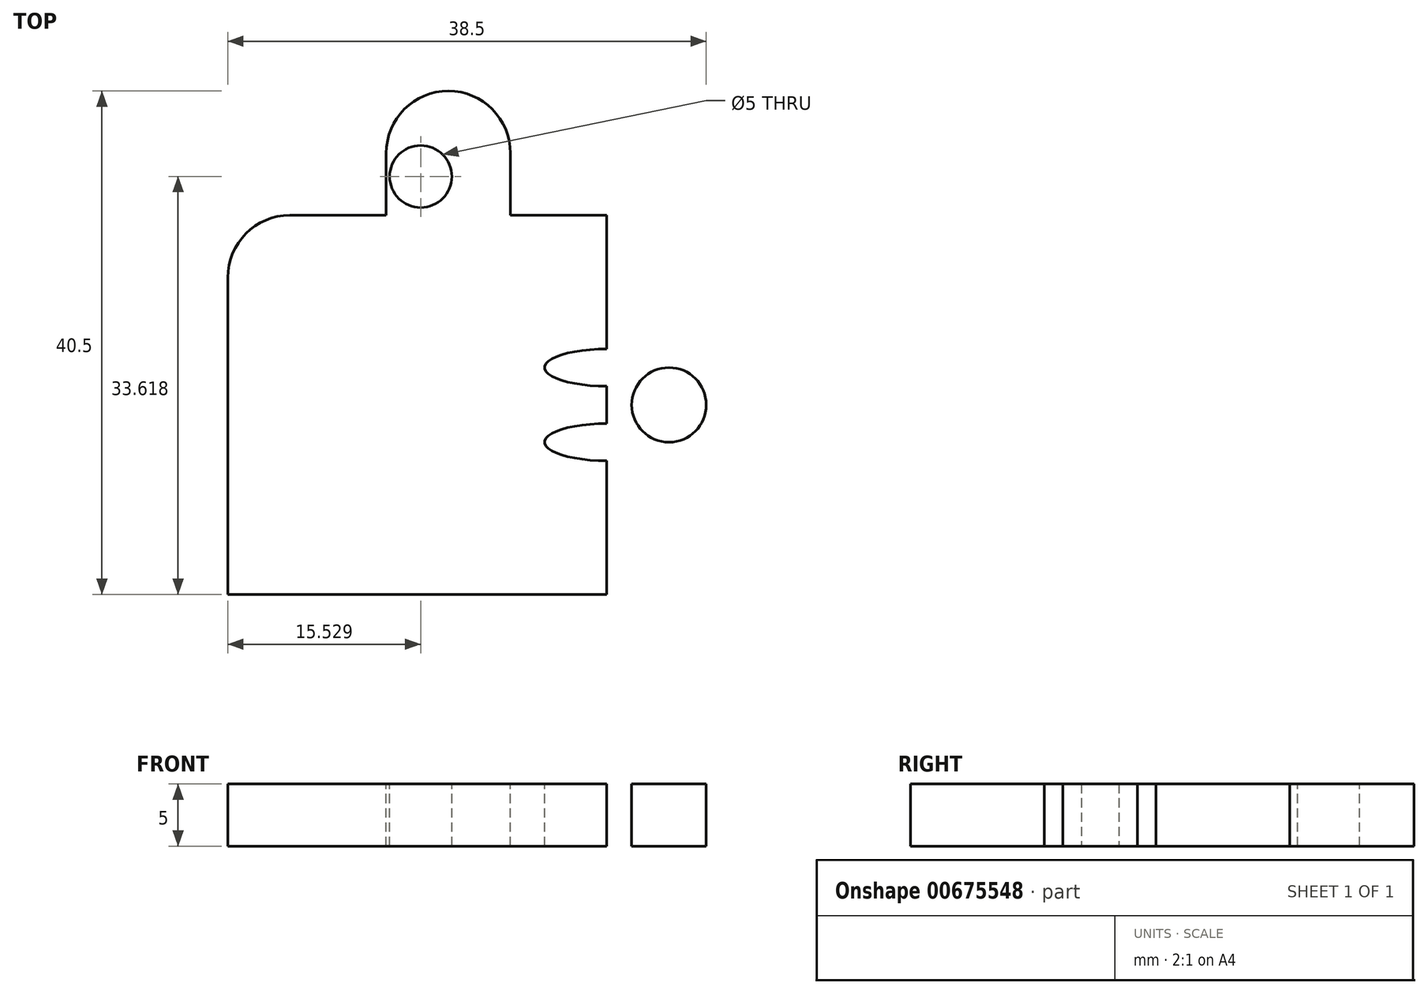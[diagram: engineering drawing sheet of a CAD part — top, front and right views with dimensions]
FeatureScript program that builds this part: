
annotation { "Feature Type Name" : "Feature", "Feature Type Description" : "" }
export const myFeature = defineFeature(function(context is Context, id is Id, definition is map)
    precondition{}
    {
        {
            var Q0;
            Q0=qCreatedBy(makeId("Top.planeOp"),FACE);
            var sketch = newSketch(context, id + "F0", { "sketchPlane" : qUnion([Q0])});
            skLineSegment(sketch, "E0.top", {"start": v(-30.3, -3.55) * mm, "end": v(6.31, -3.55) * mm});
            skPoint(sketch, "E1", {"position": v(2.22, 15.69) * mm});
            skPoint(sketch, "E1.positionSnap0", {"position": v(-28.28, 15.69) * mm});
            skPoint(sketch, "E1.positionSnap1", {"position": v(2.22, 46.19) * mm});
            skLineSegment(sketch, "E2", {"start": v(2.22, 46.19) * mm, "end": v(2.22, 15.69) * mm});
            skLineSegment(sketch, "E3", {"start": v(-28.28, 15.69) * mm, "end": v(2.22, 15.69) * mm});
            skLineSegment(sketch, "E4", {"start": v(-28.28, 15.69) * mm, "end": v(-28.28, 46.19) * mm});
            skLineSegment(sketch, "E5", {"start": v(-28.28, 46.19) * mm, "end": v(2.22, 46.19) * mm});
            skLineSegment(sketch, "E6", {"start": v(2.22, 30.94) * mm, "end": v(2.22, 33.94) * mm});
            skLineSegment(sketch, "E7", {"start": v(2.22, 33.94) * mm, "end": v(2.22, 30.94) * mm});
            skLineSegment(sketch, "E8", {"start": v(2.22, 30.94) * mm, "end": v(2.22, 27.94) * mm});
            skLineSegment(sketch, "E9", {"start": v(2.22, 30.94) * mm, "end": v(2.22, 32.44) * mm});
            skLineSegment(sketch, "E10", {"start": v(2.22, 32.44) * mm, "end": v(2.22, 30.94) * mm});
            skLineSegment(sketch, "E11", {"start": v(2.22, 27.94) * mm, "end": v(2.22, 29.44) * mm});
            skEllipse(sketch, "E12", {"center": v(2.22, 27.94) * mm, "majorRadius": 1.5 * mm, "minorRadius": 5 * mm, "majorAxis": v(0, 1)});
            skEllipse(sketch, "E13", {"center": v(2.22, 33.94) * mm, "majorRadius": 1.5 * mm, "minorRadius": 5 * mm, "majorAxis": v(0, -1)});
            skLineSegment(sketch, "E14", {"start": v(2.22, 30.94) * mm, "end": v(9.22, 30.94) * mm});
            skLineSegment(sketch, "E15", {"start": v(7.22, 27.94) * mm, "end": v(7.22, 33.94) * mm});
            skEllipse(sketch, "E16", {"center": v(7.22, 30.94) * mm, "majorRadius": 3 * mm, "minorRadius": 3 * mm, "majorAxis": v(0, 1)});
            skSolve(sketch);
        }
        {
            var Q0;
            {var subQ0=sQuery(id+"F0.wireOp",EDGE,"E3");Q0=makeQuery(id+"F0.imprint","IMPRINT",FACE,{"disambiguationData":[TD([[makeQuery(id+"F0.imprint","IMPRINT",EDGE,{"derivedFrom":subQ0}),1.0]])]});}
            var Q1;
            {var subQ0=sQuery(id+"F0.wireOp",EDGE,"E7");Q1=makeQuery(id+"F0.imprint","IMPRINT",FACE,{"disambiguationData":[TD([[makeQuery(id+"F0.imprint","IMPRINT",EDGE,{"derivedFrom":subQ0}),-1.0]])]});}
            var Q2;
            {var subQ0=sQuery(id+"F0.wireOp",EDGE,"E11");Q2=makeQuery(id+"F0.imprint","IMPRINT",FACE,{"disambiguationData":[TD([[makeQuery(id+"F0.imprint","IMPRINT",EDGE,{"derivedFrom":subQ0}),1.0]])]});}
            var Q3;
            {var subQ0=sQuery(id+"F0.wireOp",EDGE,"E8");Q3=makeQuery(id+"F0.imprint","IMPRINT",FACE,{"disambiguationData":[TD([[makeQuery(id+"F0.imprint","IMPRINT",EDGE,{"derivedFrom":subQ0}),1.0]])]});}
            var Q4;
            {var subQ0=sQuery(id+"F0.wireOp",EDGE,"E10");Q4=makeQuery(id+"F0.imprint","IMPRINT",FACE,{"disambiguationData":[TD([[makeQuery(id+"F0.imprint","IMPRINT",EDGE,{"derivedFrom":subQ0}),1.0]])]});}
            var Q5;
            {var subQ0=sQuery(id+"F0.wireOp",EDGE,"E16");var subQ1=sQuery(id+"F0.wireOp",EDGE,"E13");var subQ3=makeQuery(id+"F0.imprint","INTERSECT",VERTEX,{"derivedFrom":[subQ1,subQ0]});Q5=makeQuery(id+"F0.imprint","IMPRINT",FACE,{"disambiguationData":[TD([[makeQuery(id+"F0.imprint","IMPRINT",EDGE,{"disambiguationData":[TD([[subQ3,-1.0]])],"derivedFrom":subQ1}),1.0]])]});}
            var Q6;
            {var subQ1=sQuery(id+"F0.wireOp",EDGE,"E15");var subQ5=sQuery(id+"F0.wireOp",EDGE,"E14");var subQ6=makeQuery(id+"F0.imprint","INTERSECT",VERTEX,{"derivedFrom":[subQ5,subQ1]});Q6=makeQuery(id+"F0.imprint","IMPRINT",FACE,{"disambiguationData":[TD([[makeQuery(id+"F0.imprint","IMPRINT",EDGE,{"disambiguationData":[TD([[subQ6,1.0]])],"derivedFrom":subQ5}),1.0]])]});}
            var Q7;
            {var subQ1=sQuery(id+"F0.wireOp",EDGE,"E15");var subQ5=sQuery(id+"F0.wireOp",EDGE,"E14");var subQ6=makeQuery(id+"F0.imprint","INTERSECT",VERTEX,{"derivedFrom":[subQ5,subQ1]});Q7=makeQuery(id+"F0.imprint","IMPRINT",FACE,{"disambiguationData":[TD([[makeQuery(id+"F0.imprint","IMPRINT",EDGE,{"disambiguationData":[TD([[subQ6,1.0]])],"derivedFrom":subQ5}),-1.0]])]});}
            var Q8;
            {var subQ0=sQuery(id+"F0.wireOp",EDGE,"E16");var subQ1=sQuery(id+"F0.wireOp",EDGE,"E12");var subQ3=makeQuery(id+"F0.imprint","INTERSECT",VERTEX,{"derivedFrom":[subQ1,subQ0]});Q8=makeQuery(id+"F0.imprint","IMPRINT",FACE,{"disambiguationData":[TD([[makeQuery(id+"F0.imprint","IMPRINT",EDGE,{"disambiguationData":[TD([[subQ3,1.0]])],"derivedFrom":subQ1}),1.0]])]});}
            var Q9;
            {var subQ1=sQuery(id+"F0.wireOp",EDGE,"E15");var subQ3=makeQuery(id+"F0.imprint","INTERSECT",VERTEX,{"derivedFrom":[sQuery(id+"F0.wireOp",EDGE,"E14"),subQ1]});Q9=makeQuery(id+"F0.imprint","IMPRINT",FACE,{"disambiguationData":[TD([[makeQuery(id+"F0.imprint","IMPRINT",EDGE,{"disambiguationData":[TD([[subQ3,1.0]])],"derivedFrom":subQ1}),-1.0]])]});}
            extrude(context, id + "F1", {"entities" : qUnion([Q0, Q1, Q2, Q3, Q4, Q5, Q6, Q7, Q8, Q9]), "depth" : 5 * mm, "offsetDistance" : 25 * mm});
        }
        {
            var Q0;
            Q0=makeQuery(id+"F1.opExtrude","SWEPT_EDGE",EDGE,{"disambiguationData":[OSD([sQuery(id+"F0.wireOp",EDGE,"E4"),sQuery(id+"F0.wireOp",EDGE,"E5")])]});
            fillet(context, id + "F2", {"entities" : qUnion([Q0]), "radius" : 5 * mm, "tangentPropagation" : true, "allowEdgeOverflow" : false});
        }
        {
            var Q0;
            Q0=makeQuery(id+"F1.opExtrude","SWEPT_FACE",FACE,{"disambiguationData":[OSD([sQuery(id+"F0.wireOp",EDGE,"E5")])]});
            var sketch = newSketch(context, id + "F3", { "sketchPlane" : qUnion([Q0])});
            skLineSegment(sketch, "E17", {"start": v(10.53, 5) * mm, "end": v(10.53, 0) * mm});
            skLineSegment(sketch, "E18.bottom", {"start": v(5.53, 0) * mm, "end": v(15.53, 0) * mm});
            skLineSegment(sketch, "E18.top", {"start": v(5.53, 5) * mm, "end": v(15.53, 5) * mm});
            skLineSegment(sketch, "E18.left", {"start": v(5.53, 0) * mm, "end": v(5.53, 5) * mm});
            skLineSegment(sketch, "E18.right", {"start": v(15.53, 0) * mm, "end": v(15.53, 5) * mm});
            skPoint(sketch, "E18.middle", {"position": v(10.53, 2.5) * mm});
            skSolve(sketch);
        }
        {
            var Q0;
            Q0 = qSketchRegion(id + "F3", true);
            extrude(context, id + "F4", {"entities" : qUnion([Q0]), "operationType" : NewBodyOperationType.ADD, "depth" : 10 * mm, "offsetDistance" : 25 * mm});
        }
        {
            var Q0;
            Q0=makeQuery(id+"F4.opExtrude","CAP_EDGE",EDGE,{"disambiguationData":[OSD([sQuery(id+"F3.wireOp",EDGE,"E18.right")])],"isStart":false});
            var Q1;
            Q1=makeQuery(id+"F4.opExtrude","CAP_EDGE",EDGE,{"disambiguationData":[OSD([sQuery(id+"F3.wireOp",EDGE,"E18.left")])],"isStart":false});
            fillet(context, id + "F5", {"entities" : qUnion([Q0, Q1]), "radius" : 5 * mm, "tangentPropagation" : true, "allowEdgeOverflow" : false});
        }
        {
            var Q0;
            Q0=makeQuery(id+"F4.boolean.opBoolean","MERGE",FACE,{"derivedFrom":[makeQuery(id+"F1.opExtrude","CAP_FACE",FACE,{"disambiguationData":[OSD([sQuery(id+"F0.wireOp",EDGE,"E2"),sQuery(id+"F0.wireOp",EDGE,"E3"),sQuery(id+"F0.wireOp",EDGE,"E4"),sQuery(id+"F0.wireOp",EDGE,"E5"),sQuery(id+"F0.wireOp",EDGE,"Rl2AYxye-4QGu-tSVe-kQJC-7b8gaQIrsMHC"),sQuery(id+"F0.wireOp",EDGE,"ASmOr1Yp-kdB4-3RpK-2wkR-3s545Jx22tpQ")])],"isStart":false}),makeQuery(id+"F4.opExtrude","SWEPT_FACE",FACE,{"disambiguationData":[OSD([sQuery(id+"F3.wireOp",EDGE,"E18.top")])]})]});
            var sketch = newSketch(context, id + "F6", { "sketchPlane" : qUnion([Q0])});
            skCircle(sketch, "E19", {"center": v(-12.75, 49.3) * mm, "radius": 2.5 * mm});
            skSolve(sketch);
        }
        {
            var Q0;
            Q0=makeQuery(id+"F6.imprint","IMPRINT",FACE,{"disambiguationData":[TD([[makeQuery(id+"F6.imprint","IMPRINT",EDGE,{"derivedFrom":sQuery(id+"F6.wireOp",EDGE,"E19")}),1.0]])]});
            var Q1;
            Q1 = qSketchRegion(id + "F6", true);
            extrude(context, id + "F7", {"entities" : qUnion([Q0, Q1]), "operationType" : NewBodyOperationType.REMOVE, "oppositeDirection" : true, "depth" : 25 * mm, "offsetDistance" : 25 * mm});
        }
    });
